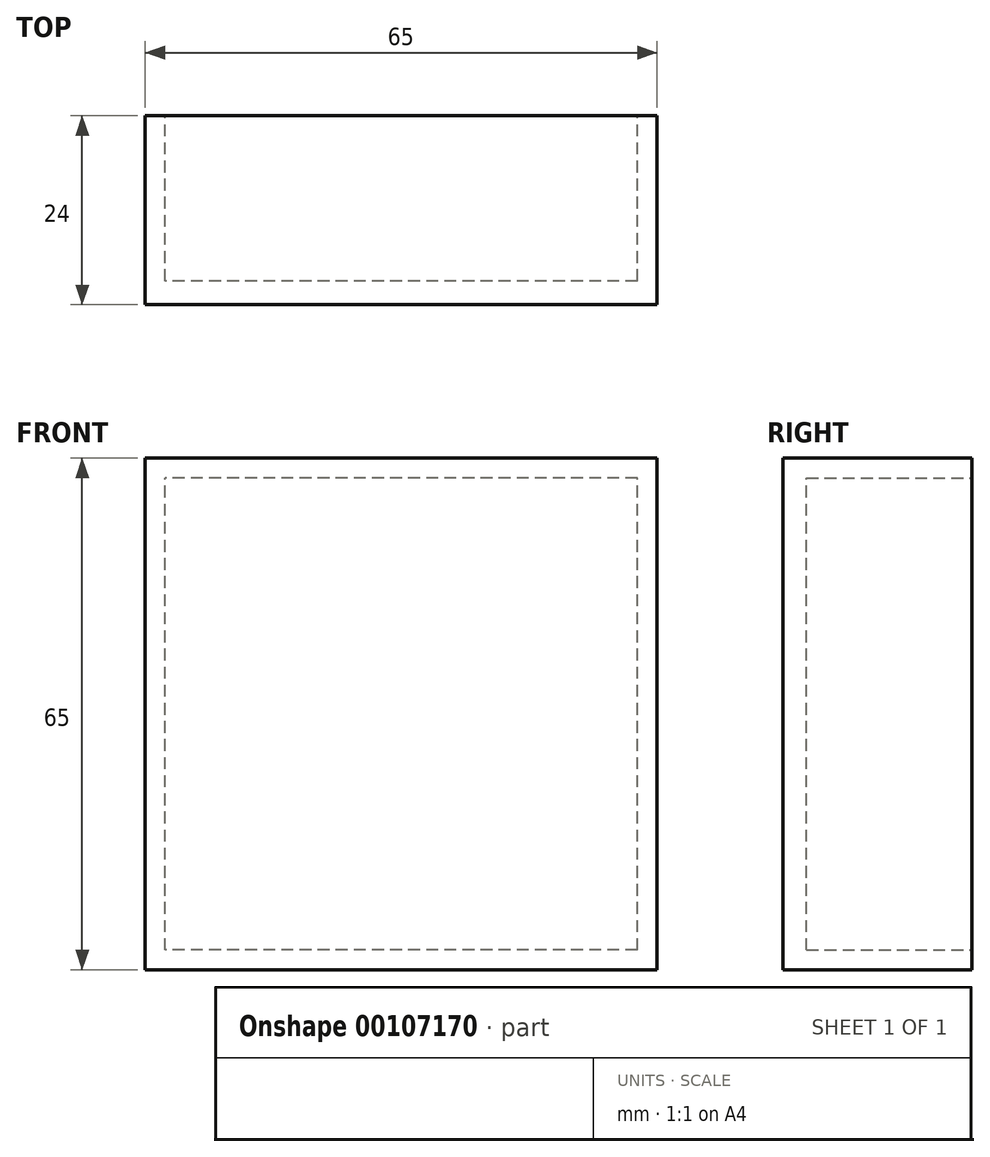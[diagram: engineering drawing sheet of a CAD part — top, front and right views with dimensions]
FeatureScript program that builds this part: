
annotation { "Feature Type Name" : "Feature", "Feature Type Description" : "" }
export const myFeature = defineFeature(function(context is Context, id is Id, definition is map)
    precondition{}
    {
        {
            var Q0;
            Q0=qCreatedBy(makeId("Front.planeOp"),FACE);
            var sketch = newSketch(context, id + "F0", { "sketchPlane" : qUnion([Q0])});
            skLineSegment(sketch, "E0.bottom", {"start": v(-36.65, 32.5) * mm, "end": v(28.35, 32.5) * mm});
            skLineSegment(sketch, "E0.top", {"start": v(-36.65, -32.5) * mm, "end": v(28.35, -32.5) * mm});
            skLineSegment(sketch, "E0.left", {"start": v(-36.65, 32.5) * mm, "end": v(-36.65, -32.5) * mm});
            skLineSegment(sketch, "E0.right", {"start": v(28.35, 32.5) * mm, "end": v(28.35, -32.5) * mm});
            skPoint(sketch, "E0.middle", {"position": v(-4.15, 0) * mm});
            skLineSegment(sketch, "E1.bottom", {"start": v(25.85, -30) * mm, "end": v(-34.15, -30) * mm});
            skLineSegment(sketch, "E1.top", {"start": v(25.85, 30) * mm, "end": v(-34.15, 30) * mm});
            skLineSegment(sketch, "E1.left", {"start": v(25.85, -30) * mm, "end": v(25.85, 30) * mm});
            skLineSegment(sketch, "E1.right", {"start": v(-34.15, -30) * mm, "end": v(-34.15, 30) * mm});
            skSolve(sketch);
        }
        {
            var Q0;
            Q0=makeQuery(id+"F0.imprint","IMPRINT",FACE,{"disambiguationData":[TD([[makeQuery(id+"F0.imprint","IMPRINT",EDGE,{"derivedFrom":sQuery(id+"F0.wireOp",EDGE,"E1.bottom")}),-1.0]])]});
            var Q1;
            Q1=makeQuery(id+"F0.imprint","IMPRINT",FACE,{"disambiguationData":[TD([[makeQuery(id+"F0.imprint","IMPRINT",EDGE,{"derivedFrom":sQuery(id+"F0.wireOp",EDGE,"E0.bottom")}),-1.0]])]});
            extrude(context, id + "F1", {"entities" : qUnion([Q0, Q1]), "depth" : 24 * mm});
        }
        {
            var Q0;
            Q0=makeQuery(id+"F0.imprint","IMPRINT",FACE,{"disambiguationData":[TD([[makeQuery(id+"F0.imprint","IMPRINT",EDGE,{"derivedFrom":sQuery(id+"F0.wireOp",EDGE,"E1.bottom")}),-1.0]])]});
            var Q1;
            Q1=sQuery(id+"F0.wireOp",EDGE,"E1.top");
            var Q2;
            Q2=sQuery(id+"F0.wireOp",EDGE,"E1.left");
            var Q3;
            Q3=sQuery(id+"F0.wireOp",EDGE,"E1.bottom");
            var Q4;
            Q4=sQuery(id+"F0.wireOp",EDGE,"E1.right");
            extrude(context, id + "F2", {"entities" : qUnion([Q0]), "operationType" : NewBodyOperationType.REMOVE, "surfaceEntities" : qUnion([Q1, Q2, Q3, Q4]), "depth" : 21 * mm});
        }
    });
